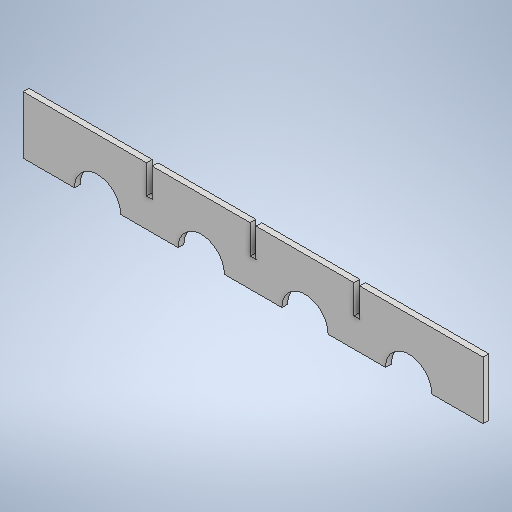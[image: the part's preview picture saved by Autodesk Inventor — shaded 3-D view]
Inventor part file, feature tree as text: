
AUTODESK INVENTOR PART (.ipt)
format: ipt  version: 2025 (Build 290162010, 162A)  size: 293,888 bytes
history: native  units: mm
features: extrude x2, sketch x2
ambient origin geometry x8: Origin, YZ Plane, XZ Plane, XY Plane, X Axis, Y Axis, Z Axis, Center Point
bodies: Solid1 (feature_tree)
feature tree (4):
  extrude  "Extrusion1"  Depth=10.0mm
  extrude  "Extrusion2"  Depth=100.0mm TaperAngle=0.0deg
  sketch  "Sketch1"  dims[d0=800.0mm d1=10.0mm]
  sketch  "Sketch2"  dims[d2=798.0mm d3=100.0mm d4=0.0mm d5=80.0mm d7=90.0mm d8=80.0mm d9=180.0mm d10=80.0mm d11=80.0mm d12=90.0mm d13=180.0mm d14=10.0mm d15=50.0mm d16=180.0mm d17=10.0mm d18=50.0mm d19=180.0mm d20=10.0mm d21=50.0mm d22=0.0mm d23=0.0mm]
